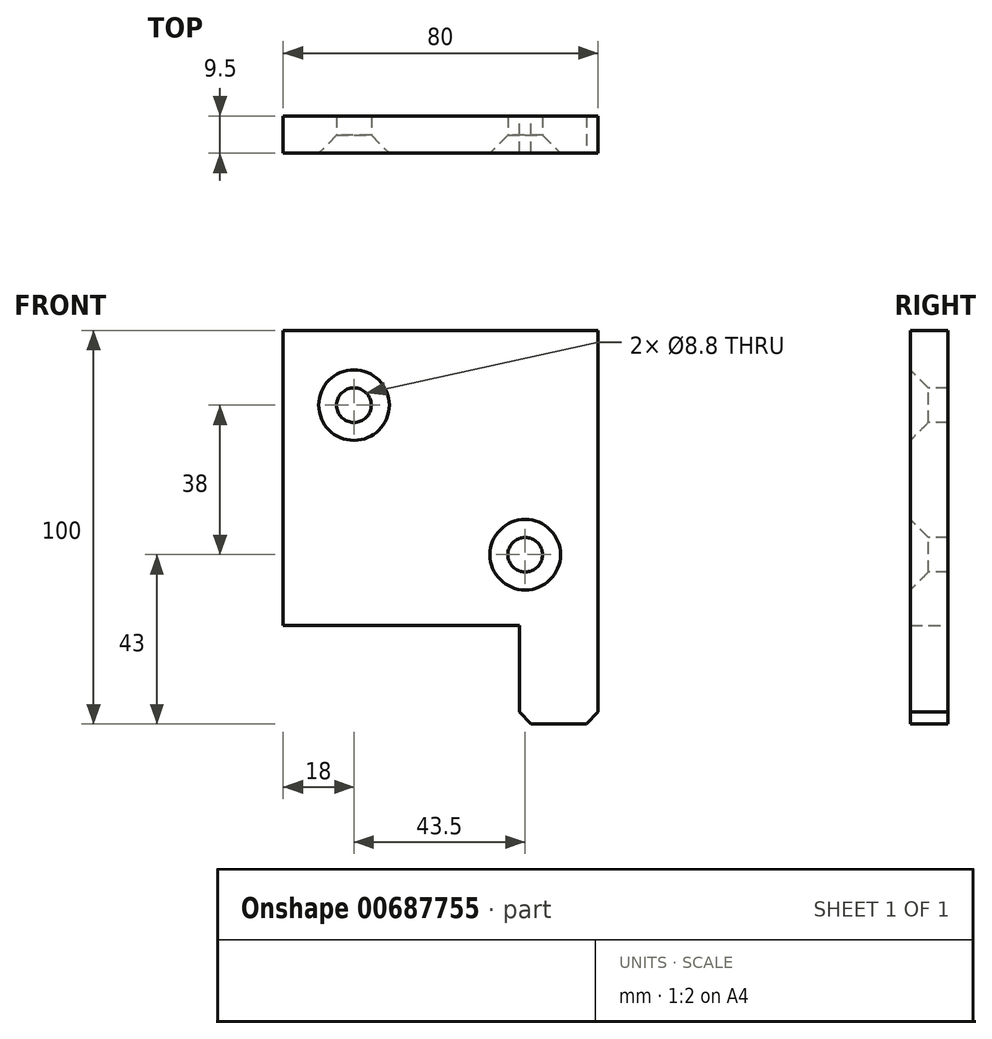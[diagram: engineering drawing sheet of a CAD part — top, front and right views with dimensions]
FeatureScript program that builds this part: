
annotation { "Feature Type Name" : "Feature", "Feature Type Description" : "" }
export const myFeature = defineFeature(function(context is Context, id is Id, definition is map)
    precondition{}
    {
        {
            var Q0;
            Q0=qCreatedBy(makeId("Front.planeOp"),FACE);
            var sketch = newSketch(context, id + "F0", { "sketchPlane" : qUnion([Q0])});
            skLineSegment(sketch, "E0", {"start": v(0, 0) * mm, "end": v(0, -100) * mm});
            skLineSegment(sketch, "E1", {"start": v(0, -100) * mm, "end": v(-20, -100) * mm});
            skLineSegment(sketch, "E2", {"start": v(-20, -100) * mm, "end": v(-20, -75) * mm});
            skLineSegment(sketch, "E3", {"start": v(-20, -75) * mm, "end": v(-80, -75) * mm});
            skLineSegment(sketch, "E4", {"start": v(-80, -75) * mm, "end": v(-80, 0) * mm});
            skLineSegment(sketch, "E5", {"start": v(-80, 0) * mm, "end": v(0, 0) * mm});
            skSolve(sketch);
        }
        {
            var Q0;
            Q0=makeQuery(id+"F0.imprint","IMPRINT",FACE,{"disambiguationData":[TD([[makeQuery(id+"F0.imprint","IMPRINT",EDGE,{"derivedFrom":sQuery(id+"F0.wireOp",EDGE,"E0")}),-1.0]])]});
            extrude(context, id + "F1", {"entities" : qUnion([Q0]), "depth" : 9.5 * mm, "offsetDistance" : 25 * mm});
        }
        {
            var Q0;
            Q0=makeQuery(id+"F1.opExtrude","CAP_FACE",FACE,{"disambiguationData":[OSD([sQuery(id+"F0.wireOp",EDGE,"E0"),sQuery(id+"F0.wireOp",EDGE,"E1"),sQuery(id+"F0.wireOp",EDGE,"E2"),sQuery(id+"F0.wireOp",EDGE,"E3"),sQuery(id+"F0.wireOp",EDGE,"E4"),sQuery(id+"F0.wireOp",EDGE,"E5")])],"isStart":false});
            var sketch = newSketch(context, id + "F2", { "sketchPlane" : qUnion([Q0])});
            skPoint(sketch, "E6", {"position": v(-18.5, -57) * mm});
            skPoint(sketch, "E7", {"position": v(-62, -19) * mm});
            skSolve(sketch);
        }
        {
            var Q0;
            Q0=sQuery(id+"F2.wireOp",VERTEX,"E7");
            var Q1;
            Q1=sQuery(id+"F2.wireOp",VERTEX,"E6");
            var Q2;
            Q2=makeQuery(id+"F1.opExtrude","SWEPT_BODY",BODY,{"disambiguationData":[OSD([sQuery(id+"F0.wireOp",EDGE,"E0"),sQuery(id+"F0.wireOp",EDGE,"E1"),sQuery(id+"F0.wireOp",EDGE,"E2"),sQuery(id+"F0.wireOp",EDGE,"E3"),sQuery(id+"F0.wireOp",EDGE,"E4"),sQuery(id+"F0.wireOp",EDGE,"E5")])]});
            hole(context, id + "F3", {"style" : HoleStyle.C_SINK, "endStyle" : HoleEndStyle.THROUGH, "standardTappedOrClearance" : lookupTablePath({ "standard" : "ISO", "fit" : "Normal", "size" : "M8", "type" : "Clearance" }), "standardBlindInLast" : lookupTablePath({ "fit" : "Standard", "standard" : "ISO", "size" : "M8", "type" : "Clearance" }), "holeDiameter" : 8.8 * mm, "cSinkDiameter" : 17.92 * mm, "cSinkAngle" : 90 * degree, "majorDiameter" : 5 * mm, "isTappedThrough" : true, "tappedDepth" : 17.25 * mm, "tapClearance" : 3, "locations" : qUnion([Q0, Q1]), "scope" : qUnion([Q2])});
        }
        {
            var Q0;
            Q0=makeQuery(id+"F1.opExtrude","SWEPT_EDGE",EDGE,{"disambiguationData":[OSD([sQuery(id+"F0.wireOp",EDGE,"E1"),sQuery(id+"F0.wireOp",EDGE,"E2")])]});
            var Q1;
            Q1=makeQuery(id+"F1.opExtrude","SWEPT_EDGE",EDGE,{"disambiguationData":[OSD([sQuery(id+"F0.wireOp",EDGE,"E0"),sQuery(id+"F0.wireOp",EDGE,"E1")])]});
            chamfer(context, id + "F4", {"entities" : qUnion([Q0, Q1]), "width" : 3 * mm, "tangentPropagation" : true});
        }
    });
